# Revit family: HOSPIVAC V4 EVISA
name_source: partatom
category: Equipement de génie climatique
revit_build: Autodesk Revit 2018 (Build: 20170223_1515(x64)
units: mm (PartAtom-declared; Revit-internal decimal feet)

## family parameters
Basée sur le plan de construction = Non
Classification = Aucun
Cote de connecteur circulaire = Utiliser le diamètre
Couper avec des vides une fois chargée = Non
Partagée = Non
Point de calcul de pièce = Non
Toujours verticalement = Oui
Type d'élément = Normal

## types (3) — shared parameters
COS_PHI = 0.9
DESCR_RESERV = Aspiration Réservoir ; G 2" MAL
DIAM_ASPI_RESEV = 50 mm  [stored 0.164042 ft]
DOUBLE_ALIMENTATION = Oui
FREQUENCE = 50 Hz
HAUT_COFF = 760 mm
LARG_COFF = 500 mm  [stored 1.64042 ft]
NBR_POLES = 3
NEUTRE = Oui
OFFSET_HAUT_TRAVERSE = 115 mm  [stored 0.377297 ft]
OFFSET_LONG_COFF = 305 mm  [stored 1.00066 ft]
OFFSET_LONG_PERC_1_PLATINE = 15 mm  [stored 0.0492126 ft]
OFFSET_LONG_PERC_4_PLATINE = 20 mm  [stored 0.0656168 ft]
TENSION_ALIM = 400 V
TERRE = Oui
Zone de maintenance 1 = Oui
Zone de maintenance coffret = Oui
ØRESERV = 50 mm  [stored 0.164042 ft]

## per-type parameters (varying)
- HOSPIVAC V4 E100: DEBIT_ASPI_VIDE=400.0 m³/h; DEBIT_REFOUL_VIDE=400.0 m³/h; DEGAG_CALORIFIQUE(kJ/h)=36381; DESCR_ALIM_X=Alimentation X ; 5G2.5mm²; DESCR_ALIM_Y=Alimentation Y ; 5G2.5mm²; DESCR_ASPI=Aspiration Vide ; 4x100 m³/h ; G 2" FEM; DESCR_REFOUL=Refoulement Vide ; 4x100 m³/h ; G 2" FEM; DIAM_ASPI_VIDE=50 mm  [stored 0.164042 ft]; DIAM_REFOUL_VIDE=50 mm  [stored 0.164042 ft]; ENTRAXE_SELLETTE=415 mm  [stored 1.36155 ft]; HAUT=863 mm  [stored 2.83136 ft]; HAUTEUR=1625 mm; HAUTEUR_AVEC_POTENCE=1730 mm; HAUT_REFOUL=96 mm; LARG=860 mm  [stored 2.82152 ft]; LARGEUR=890 mm; LARG_PLATINE=80 mm  [stored 0.262467 ft]; LONG=1720 mm; LONGUEUR=1870 mm; LONG_PLATINE_AR=120 mm  [stored 0.393701 ft]; LONG_PLATINE_AV=100 mm  [stored 0.328084 ft]; NIVEAU_SONORE(dB(A))=67; OFFSET_HAUT_CANA=689.5 mm; OFFSET_HAUT_FILTR=725 mm  [stored 2.37861 ft]; OFFSET_HAUT_PLATEAU_2=925 mm; OFFSET_HAUT_REFOUL=30 mm  [stored 0.0984252 ft]; OFFSET_HAUT_RESERV=75 mm; OFFSET_LARG_PERC_2_PLATINE=10 mm  [stored 0.0328084 ft]; OFFSET_LARG_PLATINE=15 mm  [stored 0.0492126 ft]; OFFSET_LARG_PPE=200 mm  [stored 0.656168 ft]; OFFSET_LARG_REFOUL=30 mm  [stored 0.0984252 ft]; OFFSET_LARG_RESERV=30 mm  [stored 0.0984252 ft]; OFFSET_LONG_FILTR=130 mm  [stored 0.426509 ft]; OFFSET_LONG_PERC_2_PLATINE=10 mm  [stored 0.0328084 ft]; OFFSET_LONG_PERC_3_PLATINE=15 mm  [stored 0.0492126 ft]; OFFSET_LONG_PLATINE=35 mm  [stored 0.114829 ft]; OFFSET_LONG_PPE_1=775 mm  [stored 2.54265 ft]; OFFSET_LONG_PPE_2=1400 mm; OFFSET_LONG_RESERV=1620 mm; OFFSET_TRAVERSE_PPE_A=448 mm  [stored 1.46982 ft]; OFFSET_TRAVERSE_PPE_B=1077.5 mm; POIDS(Kg)=780 mm; PROTEC_ELECT_X=Disjoncteur courbe D - 16 A; PROTEC_ELECT_Y=Disjoncteur courbe D - 16 A; PUISS_APPARENTE_X=4889 VA; PUISS_APPARENTE_Y=4889 VA; PUISS_ELECT_X=4 kW; PUISS_ELECT_Y=4 kW; SECTION_PIED=40 mm  [stored 0.131234 ft]; SECTION_TUBE=60 mm  [stored 0.19685 ft]; TYPE_FILTRATION=FILTRATION ANTI-BACTERIENNE : FD320; TYPE_POTENCE=POTENCE V4 : POTENCE V4 E100; TYPE_PPE=EVISA : f - E100.R; VISIBILITE_BRIDE=Non; VISIBILITE_FILTRATION_E300=Non; ØCOLLECTEUR=50 mm  [stored 0.164042 ft]; ØREFOUL=56 mm  [stored 0.183727 ft]
- HOSPIVAC V4 E200: DEBIT_ASPI_VIDE=800.0 m³/h; DEBIT_REFOUL_VIDE=800.0 m³/h; DEGAG_CALORIFIQUE(kJ/h)=66148; DESCR_ALIM_X=Alimentation X ; 5G4mm²; DESCR_ALIM_Y=Alimentation Y ; 5G4mm²; DESCR_ASPI=Aspiration Vide ; 4x200 m³/h ; BRIDE DN80; DESCR_REFOUL=Refoulement Vide ; 4x200 m³/h ; BRIDE DN80; DIAM_ASPI_VIDE=80 mm  [stored 0.262467 ft]; DIAM_REFOUL_VIDE=80 mm  [stored 0.262467 ft]; ENTRAXE_SELLETTE=650 mm  [stored 2.13255 ft]; HAUT=1123 mm; HAUTEUR=1890 mm; HAUTEUR_AVEC_POTENCE=2010 mm; HAUT_REFOUL=86 mm  [stored 0.282152 ft]; LARG=1150 mm; LARGEUR=1225 mm; LARG_PLATINE=100 mm  [stored 0.328084 ft]; LONG=2255 mm; LONGUEUR=2520 mm; LONG_PLATINE_AR=180 mm  [stored 0.590551 ft]; LONG_PLATINE_AV=150 mm; NIVEAU_SONORE(dB(A))=71; OFFSET_HAUT_CANA=943 mm; OFFSET_HAUT_FILTR=975 mm; OFFSET_HAUT_PLATEAU_2=1191 mm; OFFSET_HAUT_REFOUL=46 mm  [stored 0.150919 ft]; OFFSET_HAUT_RESERV=105 mm  [stored 0.344488 ft]; OFFSET_LARG_PERC_2_PLATINE=20 mm  [stored 0.0656168 ft]; OFFSET_LARG_PLATINE=5 mm  [stored 0.0164042 ft]; OFFSET_LARG_PPE=120 mm  [stored 0.393701 ft]; OFFSET_LARG_REFOUL=45 mm  [stored 0.147638 ft]; OFFSET_LARG_RESERV=45 mm  [stored 0.147638 ft]; OFFSET_LONG_FILTR=235 mm  [stored 0.770997 ft]; OFFSET_LONG_PERC_2_PLATINE=15 mm  [stored 0.0492126 ft]; OFFSET_LONG_PERC_3_PLATINE=20 mm  [stored 0.0656168 ft]; OFFSET_LONG_PLATINE=45 mm  [stored 0.147638 ft]; OFFSET_LONG_PPE_1=940 mm; OFFSET_LONG_PPE_2=1800 mm; OFFSET_LONG_RESERV=2125 mm; OFFSET_TRAVERSE_PPE_A=410 mm; OFFSET_TRAVERSE_PPE_B=1275 mm; POIDS(Kg)=1110 mm; PROTEC_ELECT_X=Disjoncteur courbe D - 25 A; PROTEC_ELECT_Y=Disjoncteur courbe D - 25 A; PUISS_APPARENTE_X=8889 VA; PUISS_APPARENTE_Y=8889 VA; PUISS_ELECT_X=8 kW; PUISS_ELECT_Y=8 kW; SECTION_PIED=60 mm  [stored 0.19685 ft]; SECTION_TUBE=90 mm  [stored 0.295276 ft]; TYPE_FILTRATION=FILTRATION ANTI-BACTERIENNE : FD600; TYPE_POTENCE=POTENCE V4 : POTENCE V4 E200; TYPE_PPE=EVISA : h - E200.R; VISIBILITE_BRIDE=Oui; VISIBILITE_FILTRATION_E300=Non; ØCOLLECTEUR=80 mm  [stored 0.262467 ft]; ØREFOUL=89 mm  [stored 0.291995 ft]
- HOSPIVAC V4 E300: DEBIT_ASPI_VIDE=1200.0 m³/h; DEBIT_REFOUL_VIDE=1200.0 m³/h; DEGAG_CALORIFIQUE(kJ/h)=90953; DESCR_ALIM_X=Alimentation X ; 5G6mm²; DESCR_ALIM_Y=Alimentation Y ; 5G6mm²; DESCR_ASPI=Aspiration Vide ; 4x300 m³/h ; BRIDE DN80; DESCR_REFOUL=Refoulement Vide ; 4x300 m³/h ; BRIDE DN80; DIAM_ASPI_VIDE=80 mm  [stored 0.262467 ft]; DIAM_REFOUL_VIDE=80 mm  [stored 0.262467 ft]; ENTRAXE_SELLETTE=650 mm  [stored 2.13255 ft]; HAUT=1123 mm; HAUTEUR=1890 mm; HAUTEUR_AVEC_POTENCE=2010 mm; HAUT_REFOUL=86 mm  [stored 0.282152 ft]; LARG=1150 mm; LARGEUR=1225 mm; LARG_PLATINE=100 mm  [stored 0.328084 ft]; LONG=2255 mm; LONGUEUR=2520 mm; LONG_PLATINE_AR=180 mm  [stored 0.590551 ft]; LONG_PLATINE_AV=150 mm; NIVEAU_SONORE(dB(A))=72; OFFSET_HAUT_CANA=943 mm; OFFSET_HAUT_FILTR=975 mm; OFFSET_HAUT_PLATEAU_2=1191 mm; OFFSET_HAUT_REFOUL=46 mm  [stored 0.150919 ft]; OFFSET_HAUT_RESERV=105 mm  [stored 0.344488 ft]; OFFSET_LARG_PERC_2_PLATINE=20 mm  [stored 0.0656168 ft]; OFFSET_LARG_PLATINE=5 mm  [stored 0.0164042 ft]; OFFSET_LARG_PPE=120 mm  [stored 0.393701 ft]; OFFSET_LARG_REFOUL=45 mm  [stored 0.147638 ft]; OFFSET_LARG_RESERV=45 mm  [stored 0.147638 ft]; OFFSET_LONG_FILTR=235 mm  [stored 0.770997 ft]; OFFSET_LONG_PERC_2_PLATINE=15 mm  [stored 0.0492126 ft]; OFFSET_LONG_PERC_3_PLATINE=20 mm  [stored 0.0656168 ft]; OFFSET_LONG_PLATINE=45 mm  [stored 0.147638 ft]; OFFSET_LONG_PPE_1=940 mm; OFFSET_LONG_PPE_2=1800 mm; OFFSET_LONG_RESERV=2125 mm; OFFSET_TRAVERSE_PPE_A=410 mm; OFFSET_TRAVERSE_PPE_B=1275 mm; POIDS(Kg)=1200 mm; PROTEC_ELECT_X=Disjoncteur courbe D - 32 A; PROTEC_ELECT_Y=Disjoncteur courbe D - 32 A; PUISS_APPARENTE_X=12222 VA; PUISS_APPARENTE_Y=12222 VA; PUISS_ELECT_X=11 kW; PUISS_ELECT_Y=11 kW; SECTION_PIED=60 mm  [stored 0.19685 ft]; SECTION_TUBE=90 mm  [stored 0.295276 ft]; TYPE_FILTRATION=FILTRATION ANTI-BACTERIENNE : FD600; TYPE_POTENCE=POTENCE V4 : POTENCE V4 E200; TYPE_PPE=EVISA : i - E300.R; VISIBILITE_BRIDE=Oui; VISIBILITE_FILTRATION_E300=Oui; ØCOLLECTEUR=80 mm  [stored 0.262467 ft]; ØREFOUL=89 mm  [stored 0.291995 ft]

note: [stored X ft] marks values corroborated as IEEE doubles in the binary element streams (Revit-internal decimal feet)

## geometry (parser evidence)
native form markers: Sweep x6
no freeform markers — native parametric forms only
